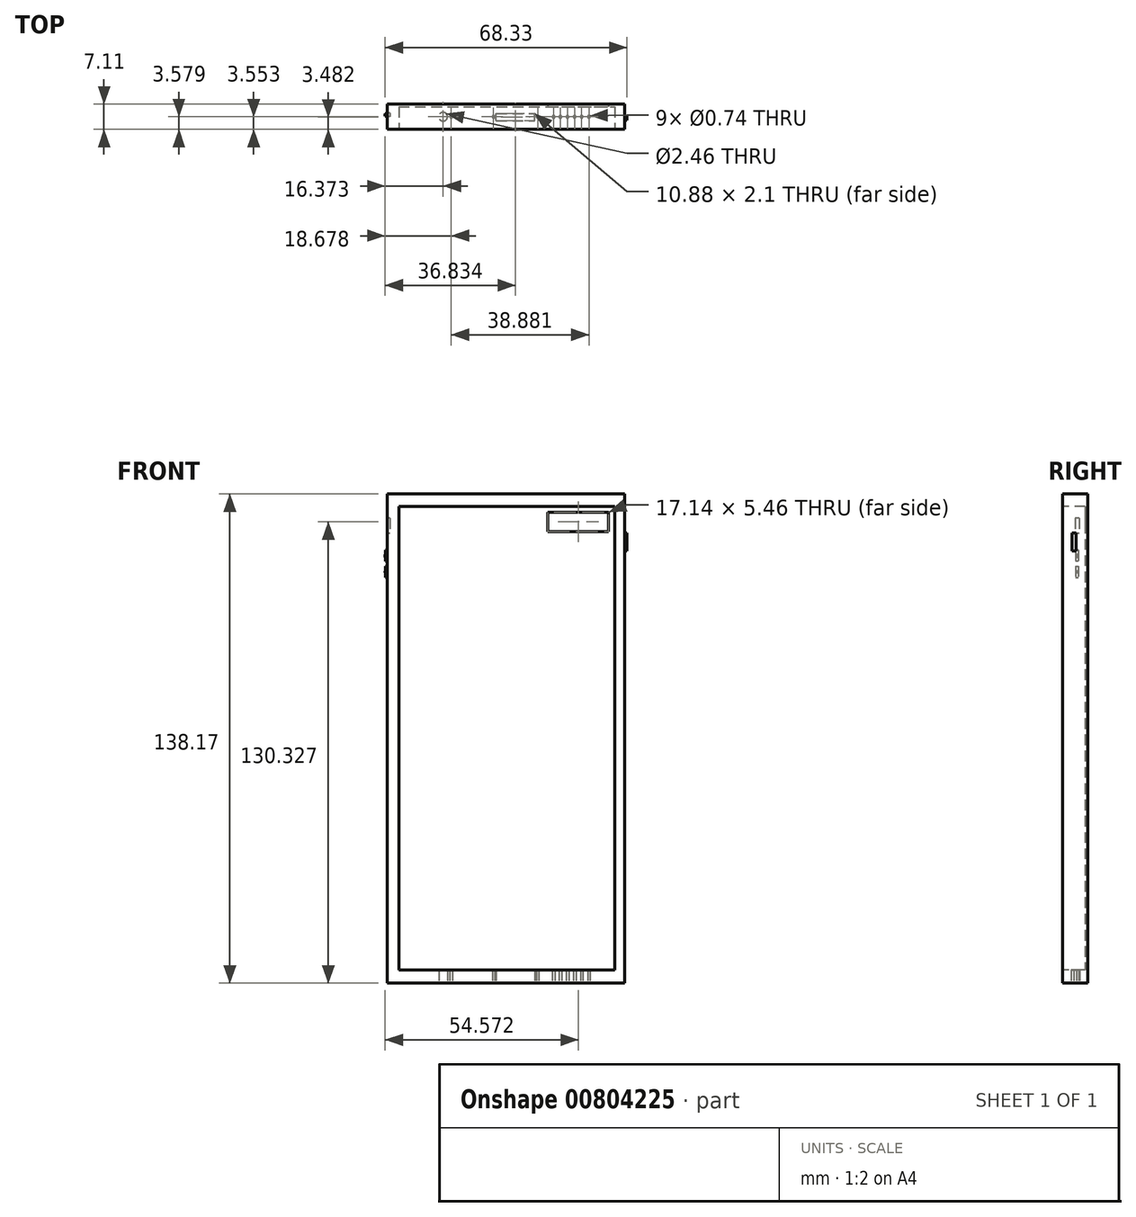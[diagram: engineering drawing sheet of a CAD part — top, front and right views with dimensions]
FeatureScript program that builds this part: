
annotation { "Feature Type Name" : "Feature", "Feature Type Description" : "" }
export const myFeature = defineFeature(function(context is Context, id is Id, definition is map)
    precondition{}
    {
        {
            var Q0;
            Q0=qCreatedBy(makeId("Front.planeOp"),FACE);
            var sketch = newSketch(context, id + "F0", { "sketchPlane" : qUnion([Q0])});
            skLineSegment(sketch, "E0.bottom", {"start": v(-45.39, 64.31) * mm, "end": v(21.67, 64.31) * mm});
            skLineSegment(sketch, "E0.top", {"start": v(-45.39, -73.86) * mm, "end": v(21.67, -73.86) * mm});
            skLineSegment(sketch, "E0.left", {"start": v(-45.39, 64.31) * mm, "end": v(-45.39, -73.86) * mm});
            skLineSegment(sketch, "E0.right", {"start": v(21.67, 64.31) * mm, "end": v(21.67, -73.86) * mm});
            skSolve(sketch);
        }
        {
            var Q0;
            Q0 = qSketchRegion(id + "F0", true);
            extrude(context, id + "F1", {"entities" : qUnion([Q0]), "depth" : 7.11 * mm, "offsetDistance" : 25.4 * mm});
        }
        {
            var Q0;
            Q0=makeQuery(id+"F1.opExtrude","SWEPT_FACE",FACE,{"disambiguationData":[OSD([sQuery(id+"F0.wireOp",EDGE,"E0.right")])]});
            var sketch = newSketch(context, id + "F2", { "sketchPlane" : qUnion([Q0])});
            skLineSegment(sketch, "E1.bottom", {"start": v(-4.49, 53.37) * mm, "end": v(-3.34, 53.37) * mm});
            skLineSegment(sketch, "E1.top", {"start": v(-4.49, 48.22) * mm, "end": v(-3.34, 48.22) * mm});
            skLineSegment(sketch, "E1.left", {"start": v(-4.49, 53.37) * mm, "end": v(-4.49, 48.22) * mm});
            skLineSegment(sketch, "E1.right", {"start": v(-3.34, 53.37) * mm, "end": v(-3.34, 48.22) * mm});
            skSolve(sketch);
        }
        {
            var Q0;
            Q0 = qSketchRegion(id + "F2", true);
            extrude(context, id + "F3", {"entities" : qUnion([Q0]), "operationType" : NewBodyOperationType.ADD, "depth" : 0.66 * mm, "offsetDistance" : 25.4 * mm});
        }
        {
            var Q0;
            Q0=makeQuery(id+"F1.opExtrude","SWEPT_FACE",FACE,{"disambiguationData":[OSD([sQuery(id+"F0.wireOp",EDGE,"E0.left")])]});
            var sketch = newSketch(context, id + "F4", { "sketchPlane" : qUnion([Q0])});
            skPoint(sketch, "E2.oppositeSnap0", {"position": v(3.56, 64.31) * mm});
            skLineSegment(sketch, "E2.bottom", {"start": v(2.47, 57.48) * mm, "end": v(3.56, 57.48) * mm});
            skLineSegment(sketch, "E2.top", {"start": v(2.47, 53.16) * mm, "end": v(3.56, 53.16) * mm});
            skLineSegment(sketch, "E2.left", {"start": v(2.47, 57.48) * mm, "end": v(2.47, 53.16) * mm});
            skLineSegment(sketch, "E2.right", {"start": v(3.56, 57.48) * mm, "end": v(3.56, 53.16) * mm});
            skSolve(sketch);
        }
        {
            var Q0;
            Q0 = qSketchRegion(id + "F4", true);
            extrude(context, id + "F5", {"entities" : qUnion([Q0]), "operationType" : NewBodyOperationType.REMOVE, "oppositeDirection" : true, "depth" : 0.79 * mm, "offsetDistance" : 25.4 * mm});
        }
        {
            var Q0;
            Q0=makeQuery(id+"F1.opExtrude","SWEPT_FACE",FACE,{"disambiguationData":[OSD([sQuery(id+"F0.wireOp",EDGE,"E0.left")])]});
            var sketch = newSketch(context, id + "F6", { "sketchPlane" : qUnion([Q0])});
            skLineSegment(sketch, "E3.bottom", {"start": v(2.63, 48.49) * mm, "end": v(3.43, 48.49) * mm});
            skLineSegment(sketch, "E3.top", {"start": v(2.63, 45.36) * mm, "end": v(3.43, 45.36) * mm});
            skLineSegment(sketch, "E3.left", {"start": v(2.63, 48.49) * mm, "end": v(2.63, 45.36) * mm});
            skLineSegment(sketch, "E3.right", {"start": v(3.43, 48.49) * mm, "end": v(3.43, 45.36) * mm});
            skLineSegment(sketch, "E4.bottom", {"start": v(3.43, 43.95) * mm, "end": v(2.63, 43.95) * mm});
            skLineSegment(sketch, "E4.top", {"start": v(3.43, 40.78) * mm, "end": v(2.63, 40.78) * mm});
            skLineSegment(sketch, "E4.left", {"start": v(3.43, 43.95) * mm, "end": v(3.43, 40.78) * mm});
            skLineSegment(sketch, "E4.right", {"start": v(2.63, 43.95) * mm, "end": v(2.63, 40.78) * mm});
            skSolve(sketch);
        }
        {
            var Q0;
            Q0 = qSketchRegion(id + "F6", true);
            extrude(context, id + "F7", {"entities" : qUnion([Q0]), "operationType" : NewBodyOperationType.ADD, "depth" : 0.48 * mm, "offsetDistance" : 25.4 * mm});
        }
        {
            var Q0;
            Q0=makeQuery(id+"F1.opExtrude","CAP_FACE",FACE,{"disambiguationData":[OSD([sQuery(id+"F0.wireOp",EDGE,"E0.bottom"),sQuery(id+"F0.wireOp",EDGE,"E0.top"),sQuery(id+"F0.wireOp",EDGE,"E0.left"),sQuery(id+"F0.wireOp",EDGE,"E0.right")])],"isStart":false});
            var sketch = newSketch(context, id + "F8", { "sketchPlane" : qUnion([Q0])});
            skLineSegment(sketch, "E5.bottom", {"start": v(-42.15, 60.79) * mm, "end": v(18.88, 60.79) * mm});
            skLineSegment(sketch, "E5.top", {"start": v(-42.15, -70.19) * mm, "end": v(18.88, -70.19) * mm});
            skLineSegment(sketch, "E5.left", {"start": v(-42.15, 60.79) * mm, "end": v(-42.15, -70.19) * mm});
            skLineSegment(sketch, "E5.right", {"start": v(18.88, 60.79) * mm, "end": v(18.88, -70.19) * mm});
            skSolve(sketch);
        }
        {
            var Q0;
            Q0 = qSketchRegion(id + "F8", true);
            extrude(context, id + "F9", {"entities" : qUnion([Q0]), "operationType" : NewBodyOperationType.REMOVE, "oppositeDirection" : true, "depth" : 6.38 * mm, "offsetDistance" : 25.4 * mm});
        }
        {
            var Q0;
            Q0=makeQuery(id+"F9.boolean.opBoolean","COPY",FACE,{"derivedFrom":makeQuery(id+"F9.opExtrude","CAP_FACE",FACE,{"disambiguationData":[OSD([sQuery(id+"F8.wireOp",EDGE,"E5.bottom"),sQuery(id+"F8.wireOp",EDGE,"E5.top"),sQuery(id+"F8.wireOp",EDGE,"E5.left"),sQuery(id+"F8.wireOp",EDGE,"E5.right")])],"isStart":false})});
            var sketch = newSketch(context, id + "F10", { "sketchPlane" : qUnion([Q0])});
            skLineSegment(sketch, "E6.bottom", {"start": v(0, 59.2) * mm, "end": v(17.14, 59.2) * mm});
            skLineSegment(sketch, "E6.top", {"start": v(0, 53.74) * mm, "end": v(17.14, 53.74) * mm});
            skLineSegment(sketch, "E6.left", {"start": v(0, 59.2) * mm, "end": v(0, 53.74) * mm});
            skLineSegment(sketch, "E6.right", {"start": v(17.14, 59.2) * mm, "end": v(17.14, 53.74) * mm});
            skSolve(sketch);
        }
        {
            var Q0;
            Q0 = qSketchRegion(id + "F10", true);
            extrude(context, id + "F11", {"entities" : qUnion([Q0]), "operationType" : NewBodyOperationType.REMOVE, "oppositeDirection" : true, "depth" : 25.4 * mm, "offsetDistance" : 25.4 * mm});
        }
        {
            var Q0;
            Q0=makeQuery(id+"F7.opExtrude","CAP_FACE",FACE,{"disambiguationData":[OSD([sQuery(id+"F6.wireOp",EDGE,"E3.bottom"),sQuery(id+"F6.wireOp",EDGE,"E3.top"),sQuery(id+"F6.wireOp",EDGE,"E3.left"),sQuery(id+"F6.wireOp",EDGE,"E3.right")])],"isStart":false});
            var sketch = newSketch(context, id + "F12", { "sketchPlane" : qUnion([Q0])});
            skText(sketch, "E7", { "text": "+", "fontName": "OpenSans-Bold.ttf"});
            const initialGuessF12  = {"E7": [0.00263, 0.04635, 1, 0, 0.00098]};
            skSetInitialGuess(sketch, initialGuessF12);
            skSolve(sketch);
        }
        {
            var Q0;
            Q0 = qSketchRegion(id + "F12", true);
            extrude(context, id + "F13", {"entities" : qUnion([Q0]), "operationType" : NewBodyOperationType.ADD, "depth" : 0.13 * mm, "offsetDistance" : 25.4 * mm});
        }
        {
            var Q0;
            Q0=makeQuery(id+"F7.opExtrude","CAP_FACE",FACE,{"disambiguationData":[OSD([sQuery(id+"F6.wireOp",EDGE,"E4.bottom"),sQuery(id+"F6.wireOp",EDGE,"E4.top"),sQuery(id+"F6.wireOp",EDGE,"E4.left"),sQuery(id+"F6.wireOp",EDGE,"E4.right")])],"isStart":false});
            var sketch = newSketch(context, id + "F14", { "sketchPlane" : qUnion([Q0])});
            skText(sketch, "E8", { "text": "-", "fontName": "OpenSans-Bold.ttf"});
            const initialGuessF14  = {"E8": [0.00263, 0.04173, 1, 0, 0.00162]};
            skSetInitialGuess(sketch, initialGuessF14);
            skSolve(sketch);
        }
        {
            var Q0;
            Q0 = qSketchRegion(id + "F14", true);
            extrude(context, id + "F15", {"entities" : qUnion([Q0]), "operationType" : NewBodyOperationType.ADD, "depth" : 0.13 * mm, "offsetDistance" : 25.4 * mm});
        }
        {
            var Q0;
            Q0=makeQuery(id+"F1.opExtrude","SWEPT_FACE",FACE,{"disambiguationData":[OSD([sQuery(id+"F0.wireOp",EDGE,"E0.top")])]});
            var sketch = newSketch(context, id + "F16", { "sketchPlane" : qUnion([Q0])});
            skCircle(sketch, "E9", {"center": v(-29.63, 3.53) * mm, "radius": 1.23 * mm});
            skSolve(sketch);
        }
        {
            var Q0;
            Q0 = qSketchRegion(id + "F16", true);
            extrude(context, id + "F17", {"entities" : qUnion([Q0]), "operationType" : NewBodyOperationType.REMOVE, "oppositeDirection" : true, "depth" : 25.4 * mm, "offsetDistance" : 25.4 * mm});
        }
        {
            var Q0;
            Q0=makeQuery(id+"F1.opExtrude","SWEPT_FACE",FACE,{"disambiguationData":[OSD([sQuery(id+"F0.wireOp",EDGE,"E0.top")])]});
            var sketch = newSketch(context, id + "F18", { "sketchPlane" : qUnion([Q0])});
            skCircle(sketch, "E10", {"center": v(-27.32, 3.56) * mm, "radius": 0.37 * mm});
            skCircle(sketch, "E11", {"center": v(-15.37, 3.56) * mm, "radius": 0.37 * mm});
            skCircle(sketch, "E12", {"center": v(-2.92, 3.56) * mm, "radius": 0.37 * mm});
            skCircle(sketch, "E13", {"center": v(1.6, 3.56) * mm, "radius": 0.37 * mm});
            skCircle(sketch, "E14", {"center": v(3.5, 3.56) * mm, "radius": 0.37 * mm});
            skCircle(sketch, "E15", {"center": v(5.5, 3.56) * mm, "radius": 0.37 * mm});
            skCircle(sketch, "E16", {"center": v(7.51, 3.56) * mm, "radius": 0.37 * mm});
            skCircle(sketch, "E17", {"center": v(9.52, 3.56) * mm, "radius": 0.37 * mm});
            skCircle(sketch, "E18", {"center": v(11.56, 3.56) * mm, "radius": 0.37 * mm});
            skSolve(sketch);
        }
        {
            var Q0;
            Q0 = qSketchRegion(id + "F18", true);
            extrude(context, id + "F19", {"entities" : qUnion([Q0]), "operationType" : NewBodyOperationType.REMOVE, "oppositeDirection" : true, "depth" : 25.4 * mm, "offsetDistance" : 25.4 * mm});
        }
        {
            var Q0;
            Q0=makeQuery(id+"F1.opExtrude","SWEPT_FACE",FACE,{"disambiguationData":[OSD([sQuery(id+"F0.wireOp",EDGE,"E0.top")])]});
            var sketch = newSketch(context, id + "F20", { "sketchPlane" : qUnion([Q0])});
            skLineSegment(sketch, "E19.bottom", {"start": v(-14.6, 4.68) * mm, "end": v(-3.72, 4.68) * mm});
            skLineSegment(sketch, "E19.top", {"start": v(-14.6, 2.58) * mm, "end": v(-3.72, 2.58) * mm});
            skLineSegment(sketch, "E19.left", {"start": v(-14.6, 4.68) * mm, "end": v(-14.6, 2.58) * mm});
            skLineSegment(sketch, "E19.right", {"start": v(-3.72, 4.68) * mm, "end": v(-3.72, 2.58) * mm});
            skSolve(sketch);
        }
        {
            var Q0;
            Q0 = qSketchRegion(id + "F20", true);
            extrude(context, id + "F21", {"entities" : qUnion([Q0]), "operationType" : NewBodyOperationType.REMOVE, "oppositeDirection" : true, "depth" : 25.4 * mm, "offsetDistance" : 25.4 * mm});
        }
        {
            var Q0;
            Q0 = qSketchRegion(id + "F18", true);
            extrude(context, id + "F22", {"entities" : qUnion([Q0]), "operationType" : NewBodyOperationType.REMOVE, "oppositeDirection" : true, "depth" : 25.4 * mm, "offsetDistance" : 25.4 * mm});
        }
    });
